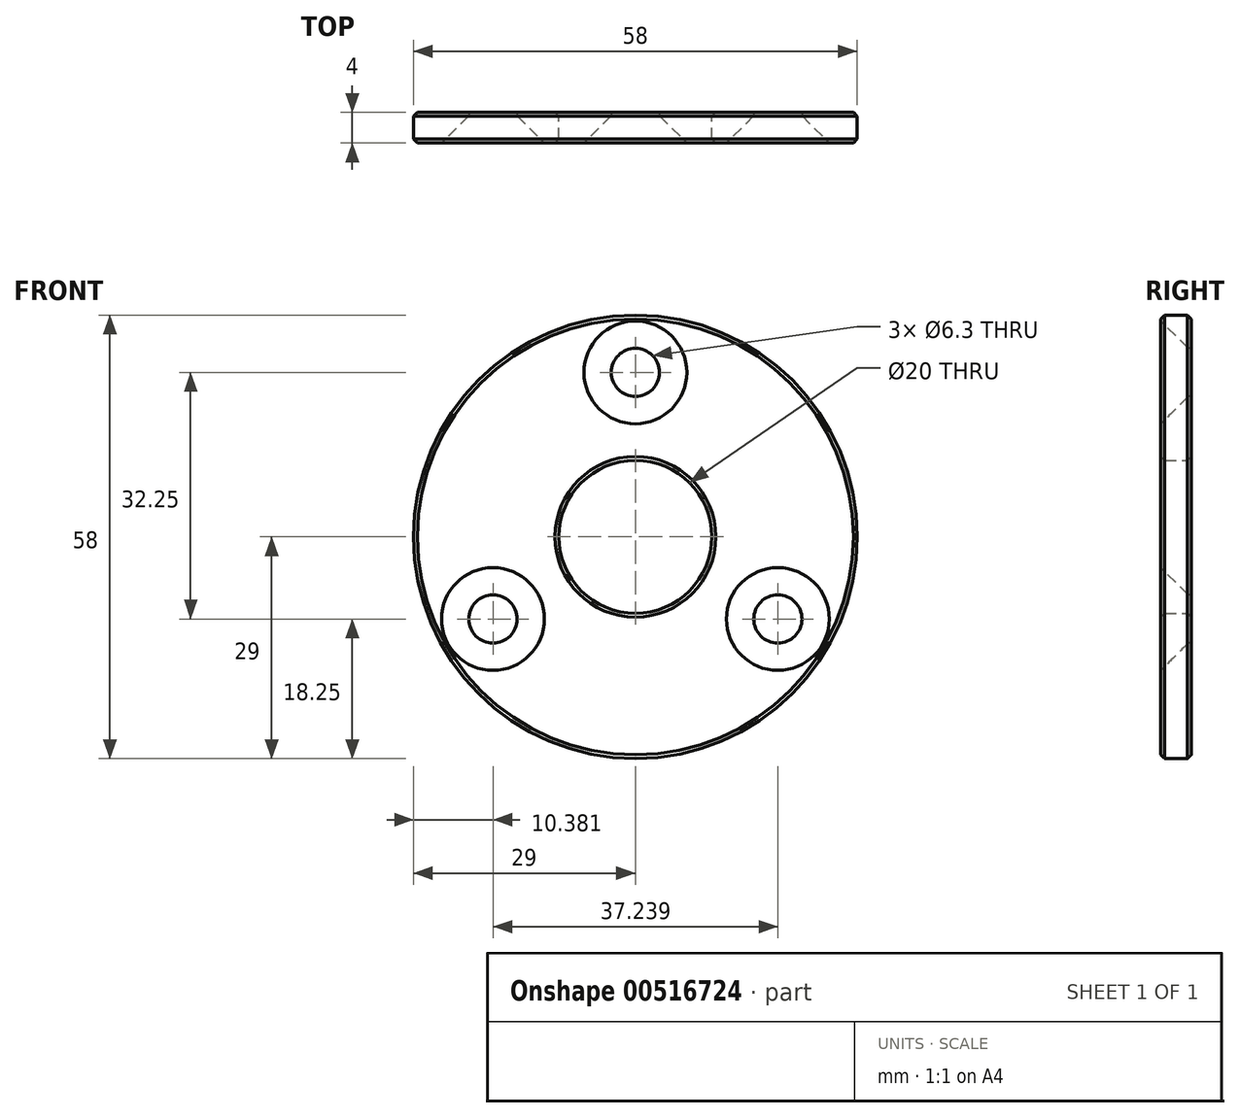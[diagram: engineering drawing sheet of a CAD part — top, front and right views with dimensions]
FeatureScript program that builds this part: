
annotation { "Feature Type Name" : "Feature", "Feature Type Description" : "" }
export const myFeature = defineFeature(function(context is Context, id is Id, definition is map)
    precondition{}
    {
        {
            var Q0;
            Q0=qCreatedBy(makeId("Front.planeOp"),FACE);
            var sketch = newSketch(context, id + "F0", { "sketchPlane" : qUnion([Q0])});
            skCircle(sketch, "E0", {"center": v(0, 0) * mm, "radius": 10 * mm});
            skCircle(sketch, "E1", {"center": v(0, 0) * mm, "radius": 29 * mm});
            skSolve(sketch);
        }
        {
            var Q0;
            Q0 = qSketchRegion(id + "F0", true);
            extrude(context, id + "F1", {"entities" : qUnion([Q0]), "depth" : 2 * mm, "offsetDistance" : 25 * mm, "hasSecondDirection" : true, "secondDirectionOppositeDirection" : true, "secondDirectionDepth" : 2 * mm});
        }
        {
            var Q0;
            Q0=makeQuery(id+"F1.opExtrude","CAP_FACE",FACE,{"disambiguationData":[OSD([sQuery(id+"F0.wireOp",EDGE,"E0"),sQuery(id+"F0.wireOp",EDGE,"E1")])],"isStart":false});
            var sketch = newSketch(context, id + "F2", { "sketchPlane" : qUnion([Q0])});
            skLineSegment(sketch, "E2", {"start": v(0, 0) * mm, "end": v(0, 29) * mm, "construction": true});
            skLineSegment(sketch, "E3", {"start": v(0, 0) * mm, "end": v(-25.11, -14.5) * mm, "construction": true});
            skLineSegment(sketch, "E4", {"start": v(0, 0) * mm, "end": v(25.11, -14.5) * mm, "construction": true});
            skPoint(sketch, "E5", {"position": v(0, 21.5) * mm});
            skPoint(sketch, "E6", {"position": v(-18.62, -10.75) * mm});
            skPoint(sketch, "E7", {"position": v(18.62, -10.75) * mm});
            skCircle(sketch, "E8", {"center": v(0, 0) * mm, "radius": 21.5 * mm, "construction": true});
            skSolve(sketch);
        }
        {
            var Q0;
            Q0=sQuery(id+"F2.wireOp",VERTEX,"E5");
            var Q1;
            Q1=sQuery(id+"F2.wireOp",VERTEX,"E6");
            var Q2;
            Q2=sQuery(id+"F2.wireOp",VERTEX,"E7");
            var Q3;
            Q3=makeQuery(id+"F1.opExtrude","SWEPT_BODY",BODY,{"disambiguationData":[OSD([sQuery(id+"F0.wireOp",EDGE,"E0"),sQuery(id+"F0.wireOp",EDGE,"E1")])]});
            hole(context, id + "F3", {"style" : HoleStyle.C_SINK, "endStyle" : HoleEndStyle.THROUGH, "standardTappedOrClearance" : lookupTablePath({ "standard" : "ISO", "fit" : "Close", "size" : "M6", "type" : "Clearance" }), "standardBlindInLast" : lookupTablePath({ "fit" : "Close", "standard" : "ISO", "size" : "M6", "type" : "Clearance" }), "holeDiameter" : 6.3 * mm, "cSinkDiameter" : 13.44 * mm, "cSinkAngle" : 90 * degree, "isTappedThrough" : true, "tappedDepth" : 12 * mm, "tapClearance" : 3, "locations" : qUnion([Q0, Q1, Q2]), "scope" : qUnion([Q3])});
        }
        {
            var Q0;
            Q0=makeQuery(id+"F1.opExtrude","CAP_EDGE",EDGE,{"disambiguationData":[OSD([sQuery(id+"F0.wireOp",EDGE,"E1")])],"isStart":false});
            var Q1;
            Q1=makeQuery(id+"F1.opExtrude","SWEPT_FACE",FACE,{"disambiguationData":[OSD([sQuery(id+"F0.wireOp",EDGE,"E1")])]});
            var Q2;
            Q2=makeQuery(id+"F1.opExtrude","CAP_EDGE",EDGE,{"disambiguationData":[OSD([sQuery(id+"F0.wireOp",EDGE,"E0")])],"isStart":true});
            var Q3;
            Q3=makeQuery(id+"F1.opExtrude","CAP_EDGE",EDGE,{"disambiguationData":[OSD([sQuery(id+"F0.wireOp",EDGE,"E0")])],"isStart":false});
            chamfer(context, id + "F4", {"entities" : qUnion([Q0, Q1, Q2, Q3]), "width" : 0.5 * mm, "tangentPropagation" : true});
        }
    });
